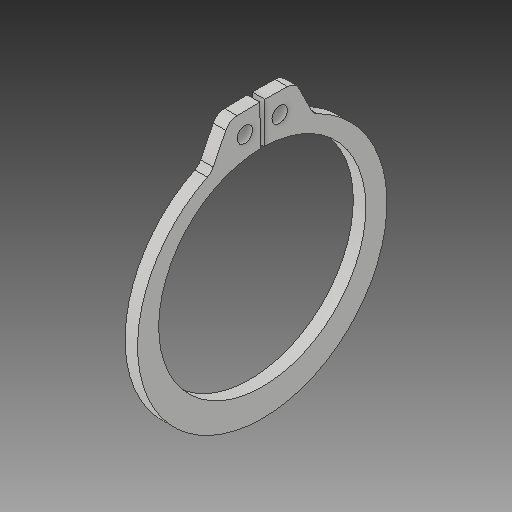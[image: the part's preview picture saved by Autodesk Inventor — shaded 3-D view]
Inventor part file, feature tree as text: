
AUTODESK INVENTOR PART (.ipt)
format: ipt  version: 2017 (Build 210142000, 142)  size: 113,664 bytes
history: native  units: in
note: dims shown in document units (in); Inventor stores cm internally (conversion verified against a paired STEP export)
features: fillet x1
ambient origin geometry x8: Origin, YZ Plane, XZ Plane, XY Plane, X Axis, Y Axis, Z Axis, Center Point
bodies: Solid1 (feature_tree)
feature tree (1):
  fillet  "Fillet1"  [1 undecoded]
note: 1 required parameter value undecoded (feature->parameter linkage not recoverable at this tier; creation-order binding heuristic only, values carry confidence <= 0.55)
